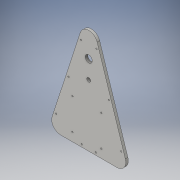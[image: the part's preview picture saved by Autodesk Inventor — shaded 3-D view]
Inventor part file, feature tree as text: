
AUTODESK INVENTOR PART (.ipt)
format: ipt  version: 2016 (Build 200138000, 138)  size: 155,648 bytes
history: native  units: in
note: dims shown in document units (in); Inventor stores cm internally (conversion verified against a paired STEP export)
features: sketch x2, extrude x2, plane x1
ambient origin geometry x8: Origin, YZ Plane, XZ Plane, XY Plane, X Axis, Y Axis, Z Axis, Center Point
bodies: Body1 (feature_tree)
feature tree (5):
  sketch  "Sketch1"  dims[d39=1.25in d40=1.25in d41=1.0in d42=1.0in d43=1.0in d44=0.4in d45=0.4in d46=0.05in d47=0.05in d48=0.4in d49=0.4in d50=0.1in d51=0.1in d52=0.1in d53=0.1in d71=2.2in]
  plane  "Work Plane1"
  sketch  "Sketch2"  dims[d73=2.05in d74=0.1in d75=0.1in d76=0.1in d77=0.1in d80=2.05in d81=0.6in d82=1.15in d84=0.5in d87=1.5in d88=0.27in d91=0.5in d92=0.5in d93=0.18in d94=0.0in d95=0.18in d96=0.0in]
  extrude  "Extrusion8"  Depth=0.05in
  extrude  "Extrusion9"  Depth=0.18in
